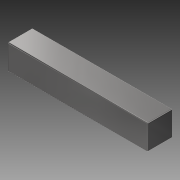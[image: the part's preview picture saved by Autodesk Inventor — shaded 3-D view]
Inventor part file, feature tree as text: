
AUTODESK INVENTOR PART (.ipt)
format: ipt  version: 2014 (Build 180170000, 170)  size: 117,248 bytes
history: native  units: mm (DEFAULTED — no unit token found)
features: other x2, sketch x1, fillet x1
ambient origin geometry x8: Origin, YZ Plane, XZ Plane, XY Plane, X Axis, Y Axis, Z Axis, Center Point
bodies: Solid1 (feature_tree), Body1 (feature_tree)
feature tree (4):
  sketch  "Sketch1"  dims[d1=17.78mm d2=-1.5875mm d3=1.5875mm d4=10.0mm d5=0.0mm d9=0.0mm d10=0.0mm d11=0.0mm d12=0.0mm d13=0.127mm]
  other  "IDS_WORKPLANE{1}"
  other  "IDS_WORKPLANE{2}"
  fillet  "Fillet1"  Radius=1.5875mm
